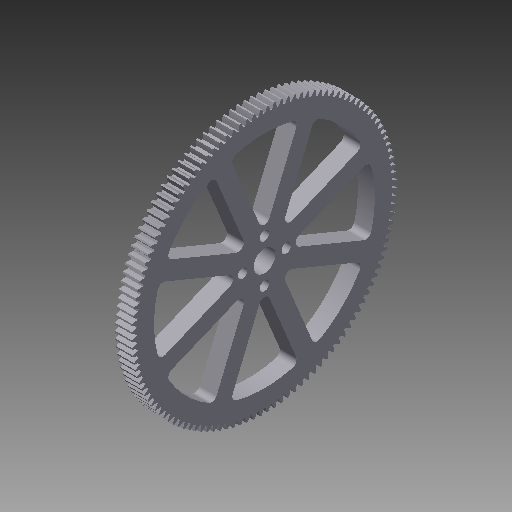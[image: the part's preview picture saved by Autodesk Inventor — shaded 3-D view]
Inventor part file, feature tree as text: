
AUTODESK INVENTOR PART (.ipt)
format: ipt  version: 2017 (Build 210142000, 142)  size: 850,944 bytes
history: native  units: in
note: dims shown in document units (in); Inventor stores cm internally (conversion verified against a paired STEP export)
features: imported_body x1, extrude x1, fillet x1, pattern_circular x1, sketch x1
ambient origin geometry x8: Origin, YZ Plane, XZ Plane, XY Plane, X Axis, Y Axis, Z Axis, Center Point
bodies: Solid1 (feature_tree)
feature tree (5):
  imported_body  "Base1"
  extrude  "Extrusion1"  Depth=0.0787in
  fillet  "Fillet1"  [1 undecoded]
  pattern_circular  "Circular Pattern1"  Angle=22.5deg  [1 undecoded]
  sketch  "Sketch1"  dims[d1=0.25in d10=0.0787in d11=22.5deg d12=22.5deg d13=0.6404in d14=0.3937in d15=0.0in d16=0.0787in d17=3.1496in d18=360.0deg]
note: 2 required parameter values undecoded (feature->parameter linkage not recoverable at this tier; creation-order binding heuristic only, values carry confidence <= 0.55)
